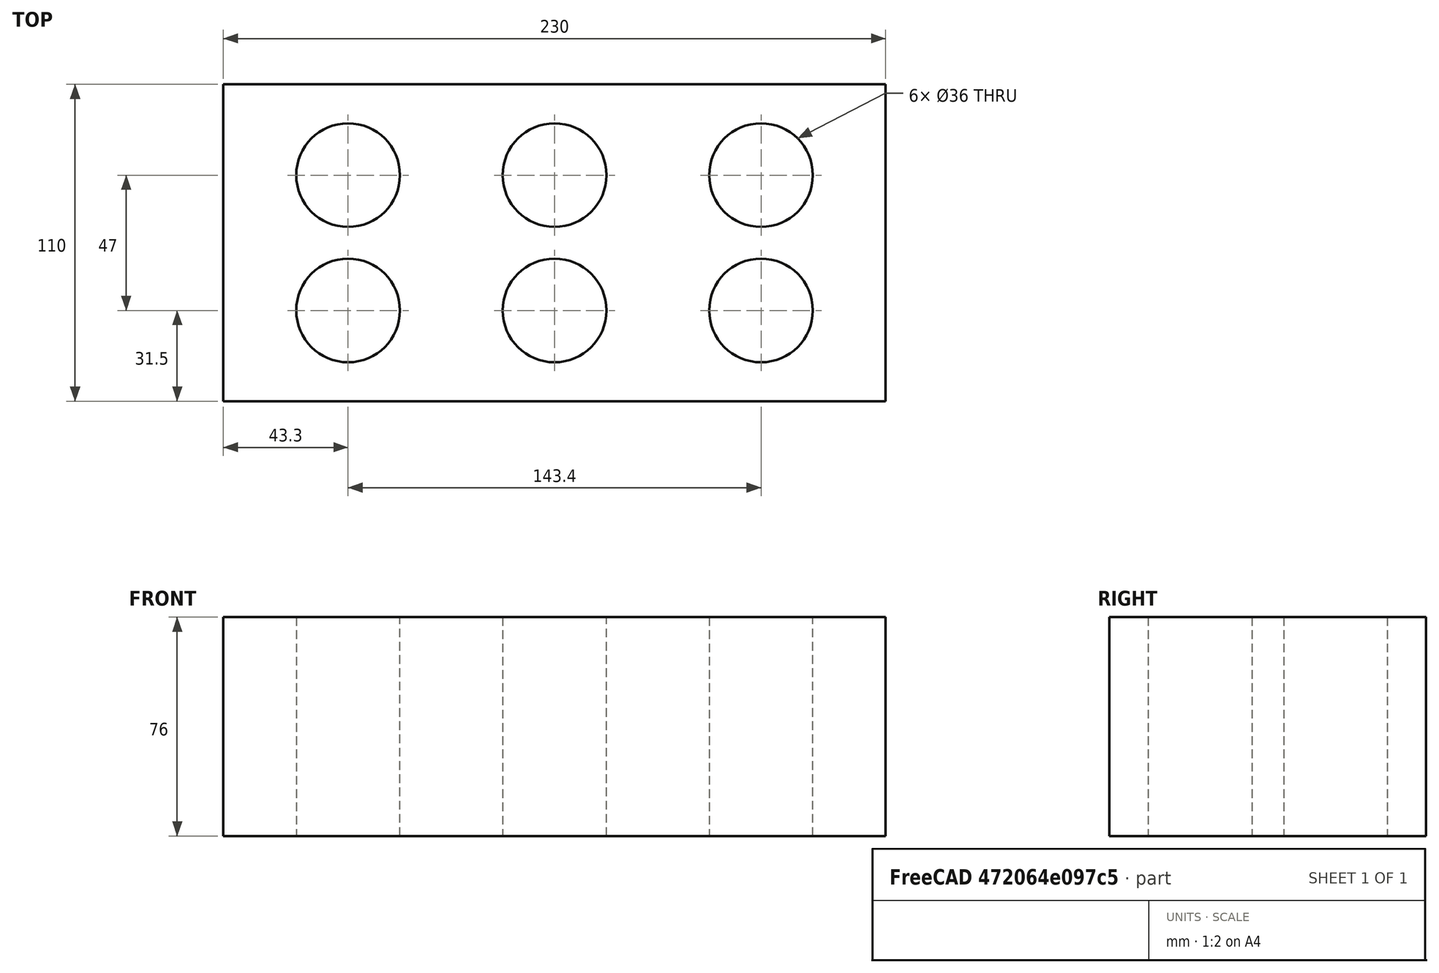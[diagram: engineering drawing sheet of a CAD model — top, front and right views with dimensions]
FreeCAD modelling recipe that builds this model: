
FCSTD DOCUMENT  (FreeCAD 1.0R39319 (Git))
Label: ojt1_t09r02_brick
License: All rights reserved
LicenseURL: https://en.wikipedia.org/wiki/All_rights_reserved
objects: Part::Cylinder×6, Part::Box×1, Part::MultiFuse×1, Part::Cut×1
note: 9 computed .brp shape members not serialized (recipe doc carries the construction recipe); baked Part::Feature solids carry a one-line shape summary decoded from their .brp

FEATURE [Part::Box] Box  label="Cube"
  AttacherType = Attacher::AttachEngine3D
  Height = 76
  Length = 230
  Width = 110
FEATURE [Part::Cylinder] Cylinder
  Angle = 360
  AttacherType = Attacher::AttachEngine3D
  FirstAngle = 0
  Height = 100
  Placement = pos=(43.3,31.5,-10) rot=(0,0,1;0rad)
  Radius = 18
  SecondAngle = 0
FEATURE [Part::Cylinder] Cylinder001
  Angle = 360
  AttacherType = Attacher::AttachEngine3D
  FirstAngle = 0
  Height = 100
  Placement = pos=(43.3,78.5,-10) rot=(0,0,1;0rad)
  Radius = 18
  SecondAngle = 0
FEATURE [Part::Cylinder] Cylinder002
  Angle = 360
  AttacherType = Attacher::AttachEngine3D
  FirstAngle = 0
  Height = 100
  Placement = pos=(115,31.5,-10) rot=(0,0,1;0rad)
  Radius = 18
  SecondAngle = 0
FEATURE [Part::Cylinder] Cylinder003
  Angle = 360
  AttacherType = Attacher::AttachEngine3D
  FirstAngle = 0
  Height = 100
  Placement = pos=(115,78.5,-10) rot=(0,0,1;0rad)
  Radius = 18
  SecondAngle = 0
FEATURE [Part::Cylinder] Cylinder004
  Angle = 360
  AttacherType = Attacher::AttachEngine3D
  FirstAngle = 0
  Height = 100
  Placement = pos=(186.7,31.5,0) rot=(0,0,1;0rad)
  Radius = 18
  SecondAngle = 0
FEATURE [Part::Cylinder] Cylinder005
  Angle = 360
  AttacherType = Attacher::AttachEngine3D
  FirstAngle = 0
  Height = 100
  Placement = pos=(186.7,78.5,-10) rot=(0,0,1;0rad)
  Radius = 18
  SecondAngle = 0
FEATURE [Part::MultiFuse] Fusion
  Refine = true
  Shapes = -> [Cylinder,Cylinder001,Cylinder002,Cylinder003,Cylinder004,Cylinder005]
FEATURE [Part::Cut] Cut
  Base = -> Box
  Refine = true
  Tool = -> Fusion
